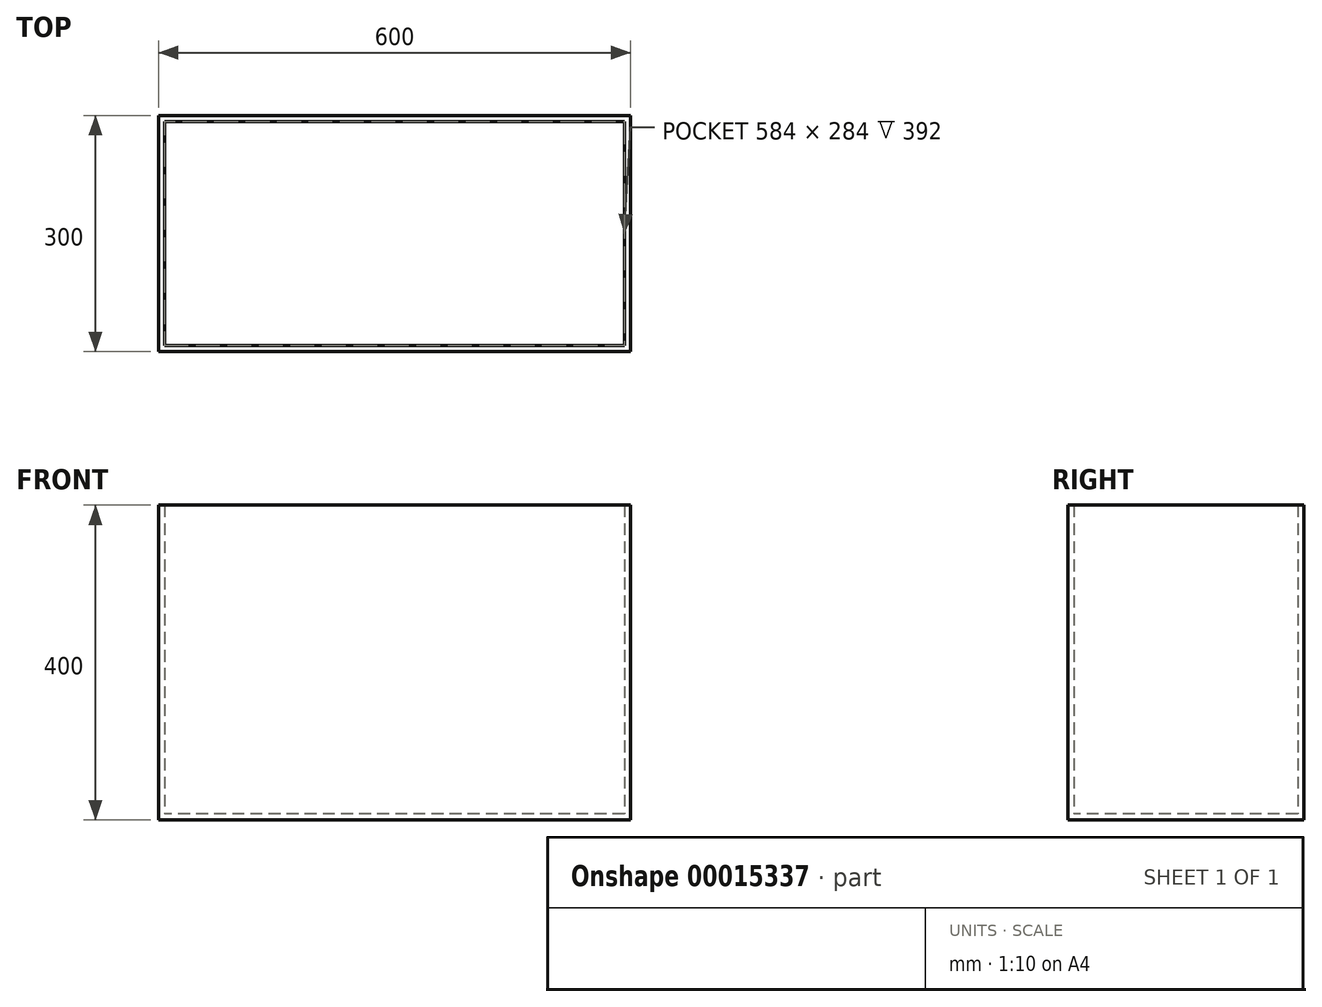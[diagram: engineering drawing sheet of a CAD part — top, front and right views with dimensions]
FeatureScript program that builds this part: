
annotation { "Feature Type Name" : "Feature", "Feature Type Description" : "" }
export const myFeature = defineFeature(function(context is Context, id is Id, definition is map)
    precondition{}
    {
        {
            var Q0;
            Q0=qCreatedBy(makeId("Top.planeOp"),FACE);
            var sketch = newSketch(context, id + "F0", { "sketchPlane" : qUnion([Q0])});
            skLineSegment(sketch, "E0.bottom", {"start": v(300, 150) * mm, "end": v(-300, 150) * mm});
            skLineSegment(sketch, "E0.top", {"start": v(300, -150) * mm, "end": v(-300, -150) * mm});
            skLineSegment(sketch, "E0.left", {"start": v(300, 150) * mm, "end": v(300, -150) * mm});
            skLineSegment(sketch, "E0.right", {"start": v(-300, 150) * mm, "end": v(-300, -150) * mm});
            skPoint(sketch, "E0.middle", {"position": v(0, 0) * mm});
            skSolve(sketch);
        }
        {
            var Q0;
            Q0 = qSketchRegion(id + "F0", true);
            extrude(context, id + "F1", {"entities" : qUnion([Q0]), "depth" : 400 * mm});
        }
        {
            var Q0;
            Q0=makeQuery(id+"F1.opExtrude","CAP_FACE",FACE,{"disambiguationData":[OSD([sQuery(id+"F0.wireOp",EDGE,"E0.bottom"),sQuery(id+"F0.wireOp",EDGE,"E0.top"),sQuery(id+"F0.wireOp",EDGE,"E0.left"),sQuery(id+"F0.wireOp",EDGE,"E0.right")])],"isStart":false});
            shell(context, id + "F2", {"entities" : qUnion([Q0]), "thickness" : 8 * mm});
        }
    });
